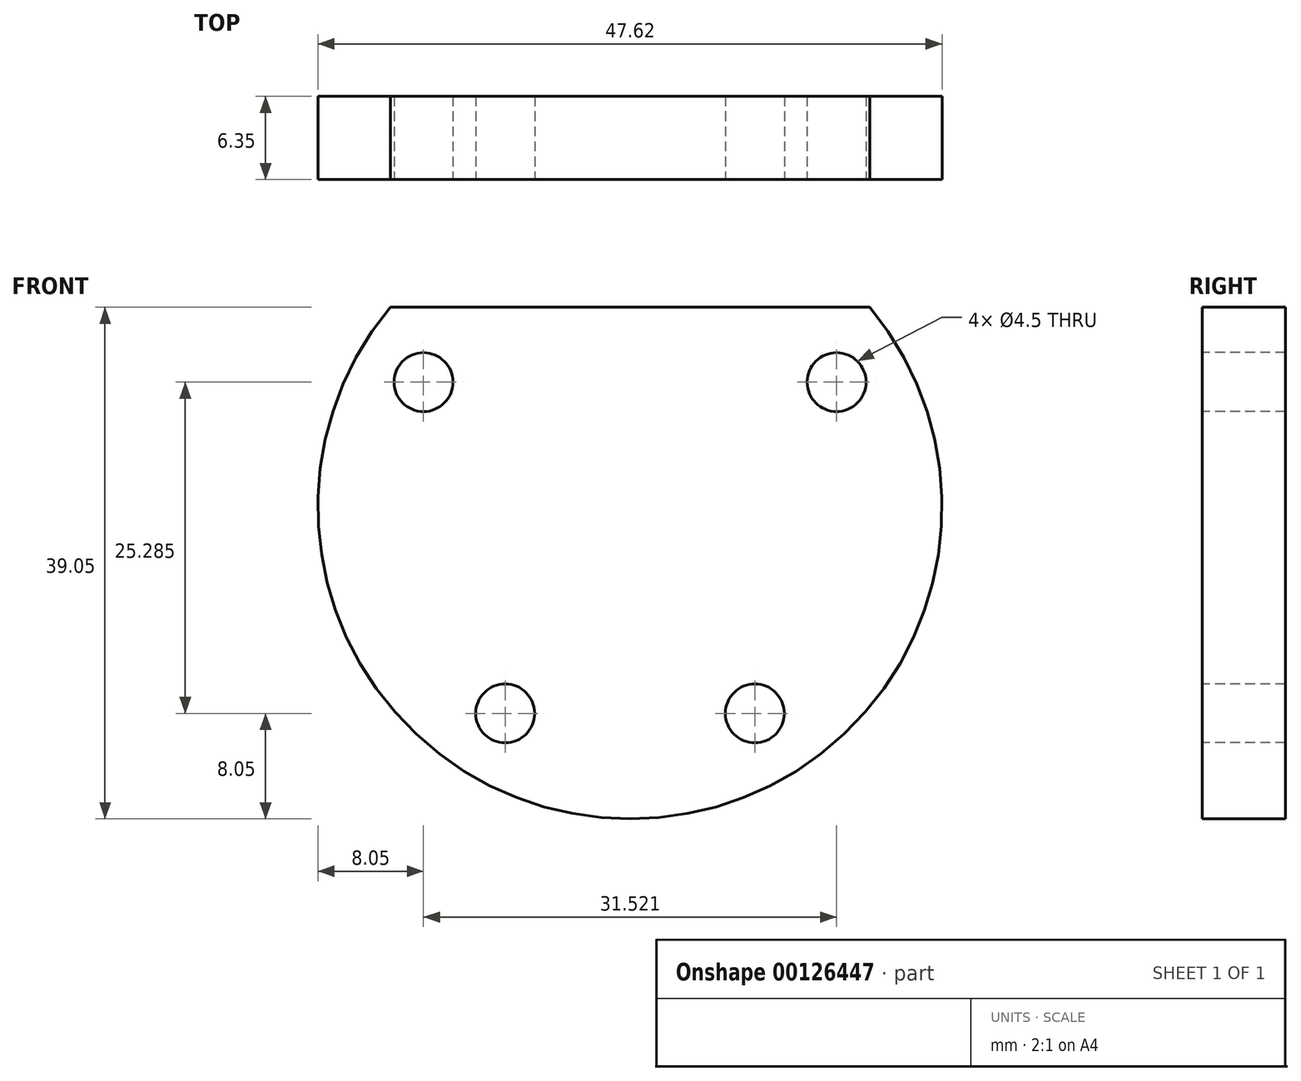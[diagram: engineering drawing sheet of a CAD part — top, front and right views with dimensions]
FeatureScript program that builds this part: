
annotation { "Feature Type Name" : "Feature", "Feature Type Description" : "" }
export const myFeature = defineFeature(function(context is Context, id is Id, definition is map)
    precondition{}
    {
        {
            var Q0;
            Q0=qCreatedBy(makeId("Front.planeOp"),FACE);
            var sketch = newSketch(context, id + "F0", { "sketchPlane" : qUnion([Q0])});
            skArc(sketch, "E0", {"start": v(-18.3, 15.24) * mm, "mid": v(0, -23.81) * mm, "end": v(18.3, 15.24) * mm});
            skLineSegment(sketch, "E1", {"start": v(-18.3, 15.24) * mm, "end": v(18.3, 15.24) * mm});
            skSolve(sketch);
        }
        {
            var Q0;
            Q0=makeQuery(id+"F0.imprint","IMPRINT",FACE,{"disambiguationData":[TD([[makeQuery(id+"F0.imprint","IMPRINT",EDGE,{"derivedFrom":sQuery(id+"F0.wireOp",EDGE,"E0")}),1.0]])]});
            extrude(context, id + "F1", {"entities" : qUnion([Q0]), "depth" : 6.35 * mm});
        }
        {
            var Q0;
            Q0=makeQuery(id+"F1.opExtrude","CAP_FACE",FACE,{"disambiguationData":[OSD([sQuery(id+"F0.wireOp",EDGE,"E0"),sQuery(id+"F0.wireOp",EDGE,"E1")])],"isStart":false});
            var sketch = newSketch(context, id + "F2", { "sketchPlane" : qUnion([Q0])});
            skCircle(sketch, "E2", {"center": v(0, 0) * mm, "radius": 18.41 * mm});
            skPoint(sketch, "E3", {"position": v(-15.76, 9.52) * mm});
            skPoint(sketch, "E4", {"position": v(15.76, 9.52) * mm});
            skPoint(sketch, "E5", {"position": v(-9.53, -15.76) * mm});
            skPoint(sketch, "E6", {"position": v(9.53, -15.76) * mm});
            skSolve(sketch);
        }
        {
            var Q0;
            Q0=sQuery(id+"F2.wireOp",VERTEX,"E3");
            var Q1;
            Q1=sQuery(id+"F2.wireOp",VERTEX,"E4");
            var Q2;
            Q2=sQuery(id+"F2.wireOp",VERTEX,"E6");
            var Q3;
            Q3=sQuery(id+"F2.wireOp",VERTEX,"E5");
            var Q4;
            Q4=makeQuery(id+"F1.opExtrude","SWEPT_BODY",BODY,{"disambiguationData":[OSD([sQuery(id+"F0.wireOp",EDGE,"E0"),sQuery(id+"F0.wireOp",EDGE,"E1")])]});
            hole(context, id + "F3", {"style" : HoleStyle.SIMPLE, "endStyle" : HoleEndStyle.THROUGH, "standardTappedOrClearance" : lookupTablePath({ "standard" : "ANSI", "fit" : "Normal (ASME)", "size" : "#8", "type" : "Clearance" }), "standardBlindInLast" : lookupTablePath({ "fit" : "Free", "standard" : "ANSI", "size" : "#8", "type" : "Clearance" }), "holeDiameter" : 4.5 * mm, "locations" : qUnion([Q0, Q1, Q2, Q3]), "scope" : qUnion([Q4]), "isTappedThrough" : true});
        }
    });
